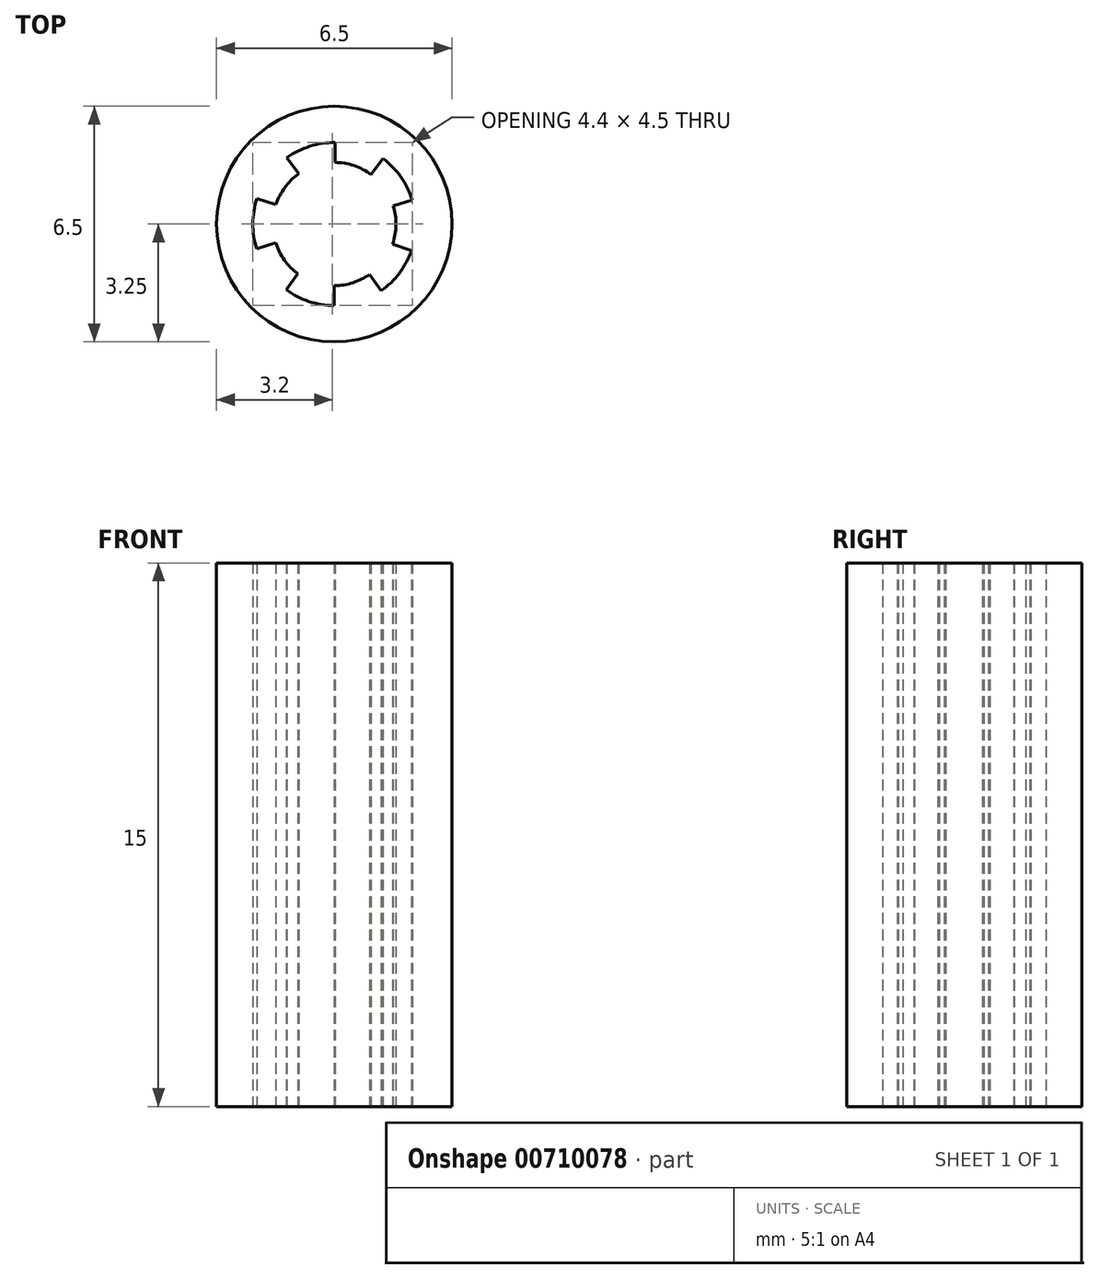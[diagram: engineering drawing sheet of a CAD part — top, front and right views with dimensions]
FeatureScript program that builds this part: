
annotation { "Feature Type Name" : "Feature", "Feature Type Description" : "" }
export const myFeature = defineFeature(function(context is Context, id is Id, definition is map)
    precondition{}
    {
        {
            var Q0;
            Q0=qCreatedBy(makeId("Top.planeOp"),FACE);
            var sketch = newSketch(context, id + "F0", { "sketchPlane" : qUnion([Q0])});
            skCircle(sketch, "E0", {"center": v(0, 0) * mm, "radius": 1.7 * mm});
            skArc(sketch, "E1", {"start": v(-2.14, 0.7) * mm, "mid": v(-2.25, 0.01) * mm, "end": v(-2.14, -0.69) * mm});
            skCircle(sketch, "E2", {"center": v(0, 0) * mm, "radius": 3.25 * mm});
            skLineSegment(sketch, "E3", {"start": v(0, -1.7) * mm, "end": v(0, -2.25) * mm});
            skLineSegment(sketch, "E4.1.0", {"start": v(-1, -1.37) * mm, "end": v(-1.33, -1.82) * mm});
            skLineSegment(sketch, "E4.2.0", {"start": v(-1.62, -0.52) * mm, "end": v(-2.14, -0.69) * mm});
            skLineSegment(sketch, "E4.3.0", {"start": v(-1.61, 0.53) * mm, "end": v(-2.14, 0.7) * mm});
            skLineSegment(sketch, "E4.4.0", {"start": v(-0.99, 1.38) * mm, "end": v(-1.3, 1.83) * mm});
            skLineSegment(sketch, "E4.5.0", {"start": v(0.02, 1.7) * mm, "end": v(0.02, 2.25) * mm});
            skLineSegment(sketch, "E4.6.0", {"start": v(1.02, 1.36) * mm, "end": v(1.34, 1.8) * mm});
            skLineSegment(sketch, "E4.7.0", {"start": v(1.62, 0.5) * mm, "end": v(2.15, 0.67) * mm});
            skLineSegment(sketch, "E4.8.0", {"start": v(1.6, -0.55) * mm, "end": v(2.13, -0.73) * mm});
            skLineSegment(sketch, "E4.9.0", {"start": v(0.98, -1.4) * mm, "end": v(1.3, -1.84) * mm});
            skLineSegment(sketch, "E4.anchor1", {"start": v(0, 0) * mm, "end": v(0, -2.25) * mm, "construction": true});
            skLineSegment(sketch, "E4.anchor2", {"start": v(0, 0) * mm, "end": v(1.3, -1.84) * mm, "construction": true});
            skArc(sketch, "E5.trimOffspring", {"start": v(0.02, 2.25) * mm, "mid": v(-0.68, 2.15) * mm, "end": v(-1.3, 1.83) * mm});
            skArc(sketch, "E6.trimOffspring", {"start": v(2.15, 0.67) * mm, "mid": v(1.84, 1.3) * mm, "end": v(1.34, 1.8) * mm});
            skArc(sketch, "E7.trimOffspring", {"start": v(1.3, -1.84) * mm, "mid": v(1.8, -1.35) * mm, "end": v(2.13, -0.73) * mm});
            skArc(sketch, "E8.trimOffspring", {"start": v(-1.33, -1.82) * mm, "mid": v(-0.7, -2.14) * mm, "end": v(0, -2.25) * mm});
            skSolve(sketch);
        }
        {
            var Q0;
            Q0 = qSketchRegion(id + "F0", true);
            extrude(context, id + "F1", {"entities" : qUnion([Q0]), "depth" : 15 * mm, "offsetDistance" : 25 * mm});
        }
    });
